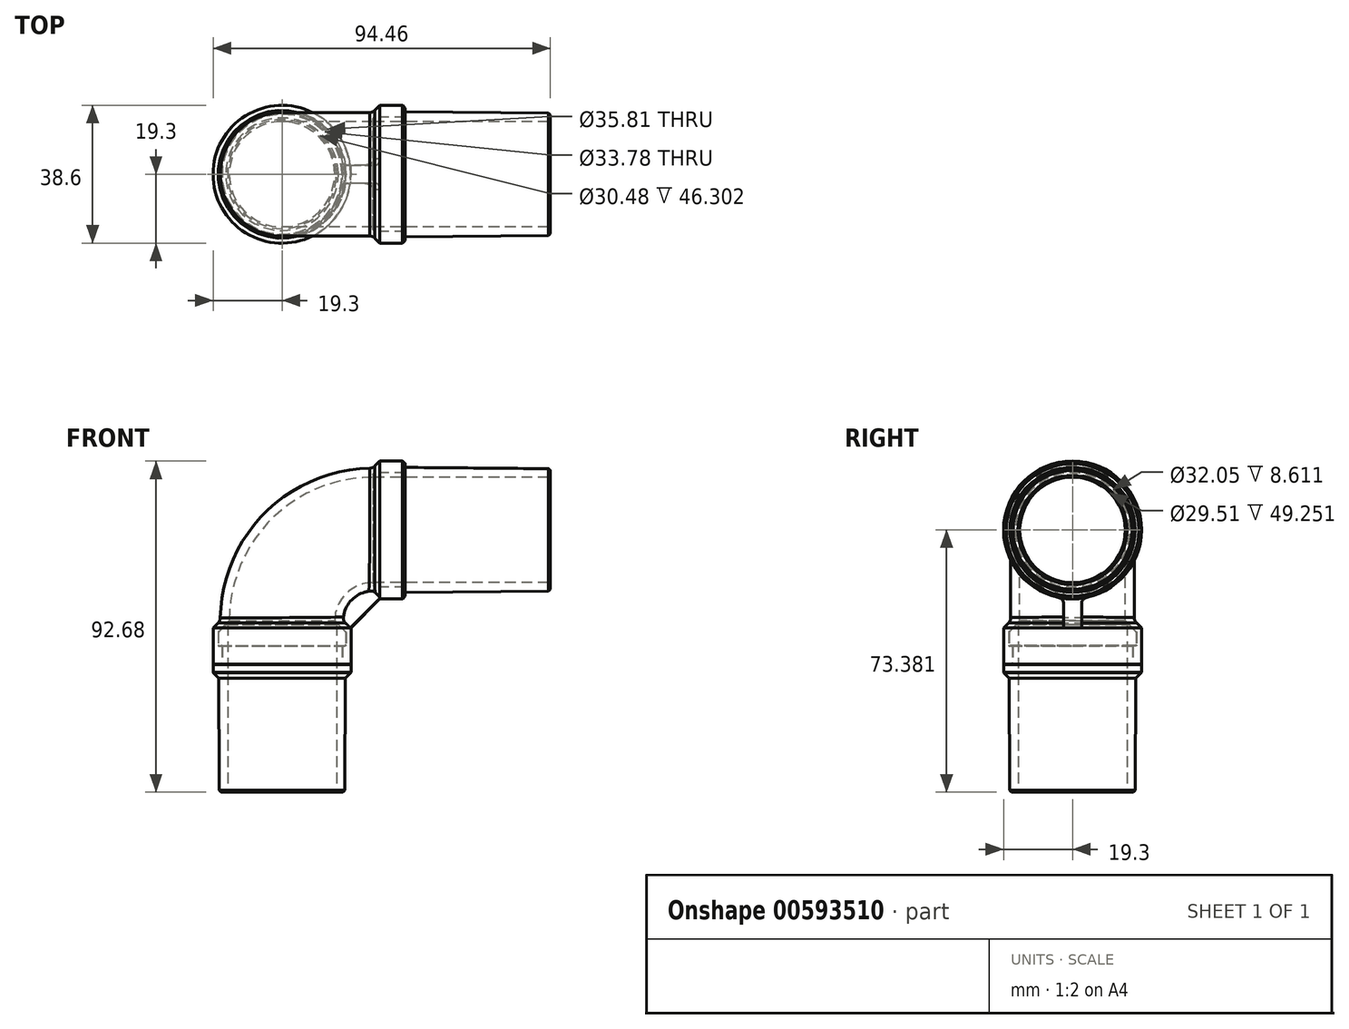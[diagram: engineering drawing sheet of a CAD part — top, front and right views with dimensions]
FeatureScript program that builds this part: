
annotation { "Feature Type Name" : "Feature", "Feature Type Description" : "" }
export const myFeature = defineFeature(function(context is Context, id is Id, definition is map)
    precondition{}
    {
        {
            var Q0;
            Q0=qCreatedBy(makeId("Front.planeOp"),FACE);
            var sketch = newSketch(context, id + "F0", { "sketchPlane" : qUnion([Q0])});
            skLineSegment(sketch, "E0.right", {"start": v(15.24, 0) * mm, "end": v(15.24, 46.81) * mm});
            skLineSegment(sketch, "E1", {"start": v(15.24, 0) * mm, "end": v(17.59, 0) * mm});
            skLineSegment(sketch, "E2.0", {"start": v(19.3, 33.45) * mm, "end": v(19.3, 35.69) * mm});
            skLineSegment(sketch, "E3", {"start": v(16.76, 36.2) * mm, "end": v(16.76, 40.77) * mm});
            skLineSegment(sketch, "E4.0", {"start": v(17.78, 41.15) * mm, "end": v(17.78, 44.62) * mm});
            skLineSegment(sketch, "E5", {"start": v(0, -5.8) * mm, "end": v(0, 47.98) * mm, "construction": true});
            skLineSegment(sketch, "E6", {"start": v(17.72, 31.88) * mm, "end": v(19.3, 33.45) * mm});
            skLineSegment(sketch, "E7.0", {"start": v(16.9, 36.2) * mm, "end": v(16.9, 40.77) * mm});
            skLineSegment(sketch, "E8.0", {"start": v(17.27, 35.81) * mm, "end": v(19.3, 35.81) * mm});
            skLineSegment(sketch, "E9", {"start": v(19.3, 35.81) * mm, "end": v(19.3, 47.98) * mm});
            skLineSegment(sketch, "E10.0", {"start": v(17.9, 41.15) * mm, "end": v(17.9, 44.62) * mm});
            skLineSegment(sketch, "E11", {"start": v(14.76, 47.98) * mm, "end": v(17.76, 44.98) * mm});
            skPoint(sketch, "E12", {"position": v(25.4, 47.98) * mm});
            skLineSegment(sketch, "E13", {"start": v(14.76, 47.98) * mm, "end": v(17.3, 47.98) * mm});
            skLineSegment(sketch, "E14", {"start": v(17.3, 47.98) * mm, "end": v(19.3, 45.97) * mm});
            skArc(sketch, "E15", {"start": v(25.4, 56.08) * mm, "mid": v(19.67, 53.71) * mm, "end": v(17.3, 47.98) * mm});
            skLineSegment(sketch, "E16", {"start": v(25.4, 54.08) * mm, "end": v(25.4, 56.08) * mm, "construction": true});
            skArc(sketch, "E17", {"start": v(25.4, 54.08) * mm, "mid": v(21.09, 52.3) * mm, "end": v(19.3, 47.98) * mm});
            skArc(sketch, "E18", {"start": v(25.4, 73.38) * mm, "mid": v(7.44, 65.94) * mm, "end": v(0, 47.98) * mm, "construction": true});
            skLineSegment(sketch, "E19", {"start": v(25.4, 56.08) * mm, "end": v(27.4, 54.08) * mm});
            skArc(sketch, "E20", {"start": v(14.76, 47.98) * mm, "mid": v(17.87, 55.5) * mm, "end": v(25.4, 58.62) * mm});
            skLineSegment(sketch, "E21", {"start": v(25.4, 54.08) * mm, "end": v(33.76, 54.08) * mm});
            skLineSegment(sketch, "E22", {"start": v(25.4, 58.62) * mm, "end": v(25.4, 56.08) * mm});
            skLineSegment(sketch, "E23.0", {"start": v(25.9, 57.35) * mm, "end": v(34.52, 57.35) * mm});
            skLineSegment(sketch, "E24.trimOffspring", {"start": v(25.4, 57.86) * mm, "end": v(25.4, 73.38) * mm, "construction": true});
            skLineSegment(sketch, "E25", {"start": v(25.4, 73.38) * mm, "end": v(54.57, 73.38) * mm, "construction": true});
            skLineSegment(sketch, "E26", {"start": v(25.4, 57.86) * mm, "end": v(25.9, 57.35) * mm});
            skLineSegment(sketch, "E27.0", {"start": v(17.59, 0) * mm, "end": v(17.72, 31.88) * mm});
            skLineSegment(sketch, "E28.0", {"start": v(34.52, 54.84) * mm, "end": v(34.52, 57.35) * mm});
            skLineSegment(sketch, "E29", {"start": v(34.52, 54.84) * mm, "end": v(33.76, 54.08) * mm});
            skLineSegment(sketch, "E30.0", {"start": v(17.27, 35.69) * mm, "end": v(19.3, 35.69) * mm});
            skLineSegment(sketch, "E31.0", {"start": v(17.02, 40.9) * mm, "end": v(17.65, 40.9) * mm});
            skLineSegment(sketch, "E32.0", {"start": v(17.02, 41.02) * mm, "end": v(17.65, 41.02) * mm});
            skLineSegment(sketch, "E33.0", {"start": v(15.75, 46.81) * mm, "end": v(17.67, 44.89) * mm});
            skLineSegment(sketch, "E34.0", {"start": v(15.75, 46.81) * mm, "end": v(15.24, 46.81) * mm});
            skArc(sketch, "E35.filletArc", {"start": v(16.9, 36.2) * mm, "mid": v(17, 35.93) * mm, "end": v(17.27, 35.81) * mm});
            skArc(sketch, "E36.filletArc", {"start": v(16.76, 36.2) * mm, "mid": v(16.91, 35.84) * mm, "end": v(17.27, 35.69) * mm});
            skArc(sketch, "E37.filletArc", {"start": v(17.02, 41.02) * mm, "mid": v(16.84, 40.95) * mm, "end": v(16.76, 40.77) * mm});
            skArc(sketch, "E38.filletArc", {"start": v(17.02, 40.9) * mm, "mid": v(16.93, 40.86) * mm, "end": v(16.9, 40.77) * mm});
            skArc(sketch, "E39.filletArc", {"start": v(17.65, 41.02) * mm, "mid": v(17.74, 41.06) * mm, "end": v(17.78, 41.15) * mm});
            skArc(sketch, "E40.filletArc", {"start": v(17.65, 40.9) * mm, "mid": v(17.83, 40.97) * mm, "end": v(17.9, 41.15) * mm});
            skPoint(sketch, "E41.visualSharp", {"position": v(17.9, 44.83) * mm});
            skArc(sketch, "E41.filletArc", {"start": v(17.9, 44.62) * mm, "mid": v(17.87, 44.81) * mm, "end": v(17.76, 44.98) * mm});
            skPoint(sketch, "E42.visualSharp", {"position": v(17.78, 44.78) * mm});
            skArc(sketch, "E42.filletArc", {"start": v(17.78, 44.62) * mm, "mid": v(17.75, 44.77) * mm, "end": v(17.67, 44.89) * mm});
            skSolve(sketch);
        }
        {
            var Q0;
            Q0=makeQuery(id+"F0.imprint","IMPRINT",FACE,{"disambiguationData":[TD([[makeQuery(id+"F0.imprint","IMPRINT",EDGE,{"derivedFrom":sQuery(id+"F0.wireOp",EDGE,"E0.right")}),-1.0]])]});
            var Q1;
            Q1=sQuery(id+"F0.wireOp",EDGE,"E5");
            revolve(context, id + "F1", {"entities" : qUnion([Q0]), "axis" : qUnion([Q1]), "revolveType" : RevolveType.FULL});
        }
        {
            var Q0;
            Q0=makeQuery(id+"F1.opRevolve","SWEPT_FACE",FACE,{"disambiguationData":[OSD([sQuery(id+"F0.wireOp",EDGE,"E1")])]});
            chamfer(context, id + "F2", {"entities" : qUnion([Q0]), "width" : 0.5 * mm, "tangentPropagation" : true});
        }
        {
            var Q0;
            Q0=makeQuery(id+"F0.imprint","IMPRINT",FACE,{"disambiguationData":[TD([[makeQuery(id+"F0.imprint","IMPRINT",EDGE,{"derivedFrom":sQuery(id+"F0.wireOp",EDGE,"E7.0")}),-1.0]])]});
            var Q1;
            Q1=sQuery(id+"F0.wireOp",EDGE,"E5");
            revolve(context, id + "F3", {"entities" : qUnion([Q0]), "axis" : qUnion([Q1]), "revolveType" : RevolveType.FULL});
        }
        {
            var Q0;
            Q0=sQuery(id+"F0.wireOp",VERTEX,"E12");
            var Q1;
            Q1=qCreatedBy(makeId("Top.planeOp"),FACE);
            cPlane(context, id + "F4", {"entities" : qUnion([Q0, Q1]), "cplaneType" : CPlaneType.PLANE_POINT, "offset" : 0 * mm, "width" : 152.4 * mm, "height" : 152.4 * mm});
        }
        {
            var Q0;
            Q0=qCreatedBy(id+"F4.planeOp",FACE);
            var sketch = newSketch(context, id + "F5", { "sketchPlane" : qUnion([Q0])});
            skPoint(sketch, "E43.0", {"position": v(25.4, 0) * mm});
            skLineSegment(sketch, "E44", {"start": v(25.4, 0) * mm, "end": v(25.4, 27.74) * mm, "construction": true});
            skLineSegment(sketch, "E45", {"start": v(25.4, 0) * mm, "end": v(44.16, 0) * mm, "construction": true});
            skSolve(sketch);
        }
        {
            var Q0;
            Q0=makeQuery(id+"F3.opRevolve","SWEPT_FACE",FACE,{"disambiguationData":[OSD([sQuery(id+"F0.wireOp",EDGE,"E13")])]});
            var Q1;
            Q1=sQuery(id+"F5.wireOp",EDGE,"E44");
            revolve(context, id + "F6", {"operationType" : NewBodyOperationType.ADD, "entities" : qUnion([Q0]), "axis" : qUnion([Q1]), "revolveType" : RevolveType.ONE_DIRECTION, "angle" : 90 * degree});
        }
        {
            var Q0;
            {var subQ0=sQuery(id+"F0.wireOp",EDGE,"E19");Q0=makeQuery(id+"F0.imprint","IMPRINT",FACE,{"disambiguationData":[TD([[makeQuery(id+"F0.imprint","IMPRINT",EDGE,{"derivedFrom":subQ0}),1.0]])]});}
            var Q1;
            Q1=sQuery(id+"F0.wireOp",EDGE,"E25");
            revolve(context, id + "F7", {"operationType" : NewBodyOperationType.ADD, "entities" : qUnion([Q0]), "axis" : qUnion([Q1]), "revolveType" : RevolveType.FULL});
        }
        {
            var Q0;
            Q0=qCreatedBy(makeId("Front.planeOp"),FACE);
            var sketch = newSketch(context, id + "F8", { "sketchPlane" : qUnion([Q0])});
            skLineSegment(sketch, "E46", {"start": v(25.4, 58.62) * mm, "end": v(75.16, 58.62) * mm});
            skLineSegment(sketch, "E47", {"start": v(34.52, 57.35) * mm, "end": v(25.9, 57.35) * mm});
            skLineSegment(sketch, "E48.0.0", {"start": v(25.4, 58.62) * mm, "end": v(25.4, 57.86) * mm});
            skPoint(sketch, "E49.orphan", {"position": v(28.17, 91.92) * mm});
            skPoint(sketch, "E50.orphan", {"position": v(28.17, 54.84) * mm});
            skLineSegment(sketch, "E51.0", {"start": v(25.4, 57.86) * mm, "end": v(25.9, 57.35) * mm});
            skLineSegment(sketch, "E52.0", {"start": v(34.52, 57.35) * mm, "end": v(34.52, 55.87) * mm});
            skLineSegment(sketch, "E53.0", {"start": v(75.16, 56.24) * mm, "end": v(75.16, 58.62) * mm});
            skLineSegment(sketch, "E54", {"start": v(75.16, 56.24) * mm, "end": v(34.52, 55.87) * mm});
            skSolve(sketch);
        }
        {
            var Q0;
            Q0=makeQuery(id+"F8.imprint","IMPRINT",FACE,{"disambiguationData":[TD([[makeQuery(id+"F8.imprint","IMPRINT",EDGE,{"derivedFrom":sQuery(id+"F8.wireOp",EDGE,"E46")}),-1.0]])]});
            var Q1;
            Q1=sQuery(id+"F0.wireOp",EDGE,"E25");
            revolve(context, id + "F9", {"entities" : qUnion([Q0]), "axis" : qUnion([Q1]), "revolveType" : RevolveType.FULL});
        }
        {
            var Q0;
            Q0=makeQuery(id+"F9.opRevolve","SWEPT_FACE",FACE,{"disambiguationData":[OSD([sQuery(id+"F8.wireOp",EDGE,"E53.0")])]});
            chamfer(context, id + "F10", {"entities" : qUnion([Q0]), "width" : 0.5 * mm, "tangentPropagation" : true});
        }
        {
            var Q0;
            Q0=sQuery(id+"F0.wireOp",EDGE,"E19");
            cPlane(context, id + "F11", {"entities" : qUnion([Q0]), "cplaneType" : CPlaneType.LINE_ANGLE, "offset" : 25.4 * mm, "angle" : 90 * degree, "width" : 152.4 * mm, "height" : 152.4 * mm});
        }
        {
            var Q0;
            Q0=qCreatedBy(id+"F11.planeOp",FACE);
            var sketch = newSketch(context, id + "F12", { "sketchPlane" : qUnion([Q0])});
            skEllipticalArc(sketch, "E55.0", {});
            skLineSegment(sketch, "E56.0", {"start": v(-2.54, 23.65) * mm, "end": v(-2.54, 18.98) * mm});
            skLineSegment(sketch, "E57.0", {"start": v(2.54, 23.65) * mm, "end": v(2.54, 18.98) * mm});
            skEllipticalArc(sketch, "E58.0", {});
            const initialGuessF12  = {"E55.0": [0, 0.032508527184401385, 1, 0, 0.019304, 0.013649989304025105, 4.580427372724815, 4.844350588044565], "E58.0": [0, 0.03392740765153032, 1, 0, 0.014757399999999999, 0.010435057612682356, 4.539410601107297, 4.88536735966208]};
            skSetInitialGuess(sketch, initialGuessF12);
            skSolve(sketch);
        }
        {
            var Q0;
            Q0=makeQuery(id+"F12.imprint","IMPRINT",FACE,{"disambiguationData":[TD([[makeQuery(id+"F12.imprint","IMPRINT",EDGE,{"derivedFrom":sQuery(id+"F12.wireOp",EDGE,"E55.0")}),1.0]])]});
            extrude(context, id + "F13", {"entities" : qUnion([Q0]), "operationType" : NewBodyOperationType.ADD, "depth" : 0.76 * mm, "offsetDistance" : 25.4 * mm});
        }
        {
            var Q0;
            Q0=makeQuery(id+"F12.imprint","IMPRINT",FACE,{"disambiguationData":[TD([[makeQuery(id+"F12.imprint","IMPRINT",EDGE,{"derivedFrom":sQuery(id+"F12.wireOp",EDGE,"E55.0")}),1.0]])]});
            extrude(context, id + "F14", {"entities" : qUnion([Q0]), "operationType" : NewBodyOperationType.ADD, "endBound" : BoundingType.UP_TO_NEXT, "oppositeDirection" : true, "depth" : 25.4 * mm, "offsetDistance" : 25.4 * mm});
        }
        {
            var Q0;
            {var subQ0=sQuery(id+"F12.wireOp",EDGE,"E56.0");Q0=makeQuery(id+"F14.boolean.opBoolean","MERGE",FACE,{"derivedFrom":[makeQuery(id+"F13.opExtrude","SWEPT_FACE",FACE,{"disambiguationData":[OSD([subQ0])]}),makeQuery(id+"F14.opExtrude","SWEPT_FACE",FACE,{"disambiguationData":[OSD([subQ0])]})]});}
            extrude(context, id + "F15", {"entities" : qUnion([Q0]), "operationType" : NewBodyOperationType.ADD, "oppositeDirection" : true, "depth" : 5.08 * mm, "offsetDistance" : 25.4 * mm});
        }
        {
            var Q0;
            Q0=makeQuery(id+"F15.opExtrude","SWEPT_FACE",FACE,{"disambiguationData":[OSD([sQuery(id+"F12.wireOp",EDGE,"E56.0"),sQuery(id+"F12.wireOp",EDGE,"E58.0")])]});
            extrude(context, id + "F16", {"entities" : qUnion([Q0]), "operationType" : NewBodyOperationType.ADD, "endBound" : BoundingType.UP_TO_NEXT, "depth" : 25.4 * mm, "offsetDistance" : 25.4 * mm});
        }
        {
            var Q0;
            {var subQ0=makeQuery(id+"F6.opRevolve","SWEPT_FACE",FACE,{"disambiguationData":[OSD([sQuery(id+"F0.wireOp",EDGE,"E13"),sQuery(id+"F0.wireOp",EDGE,"E14"),sQuery(id+"F0.wireOp",EDGE,"E15")])]});var subQ1=subQ0;var subQ2=sQuery(id+"F12.wireOp",EDGE,"E58.0");var subQ3=sQuery(id+"F12.wireOp",EDGE,"E56.0");Q0=makeQuery(id+"F16.boolean.opBoolean","MERGE",EDGE,{"derivedFrom":[makeQuery(id+"F14.boolean.opBoolean","INTERSECT",EDGE,{"derivedFrom":[subQ1,makeQuery(id+"F14.opExtrude","SWEPT_FACE",FACE,{"disambiguationData":[OSD([subQ3])]})]}),makeQuery(id+"F14.opExtrude","CAP_EDGE",EDGE,{"disambiguationData":[OSD([subQ3]),topologyDisambiguationEdgeConnected([subQ0])],"isStart":false}),makeQuery(id+"F16.opExtrude","TWEAK_EDGE",EDGE,{"derivedFrom":[makeQuery(id+"F15.boolean.opBoolean","MERGE",EDGE,{"derivedFrom":[makeQuery(id+"F14.opExtrude","SWEPT_EDGE",EDGE,{"disambiguationData":[OSD([subQ3,subQ2])]}),makeQuery(id+"F15.opExtrude","CAP_EDGE",EDGE,{"disambiguationData":[OSD([subQ3,subQ2])],"isStart":true})]}),subQ1]})]});}
            var Q1;
            {var subQ0=makeQuery(id+"F6.opRevolve","SWEPT_FACE",FACE,{"disambiguationData":[OSD([sQuery(id+"F0.wireOp",EDGE,"E13"),sQuery(id+"F0.wireOp",EDGE,"E14"),sQuery(id+"F0.wireOp",EDGE,"E15")])]});var subQ1=subQ0;var subQ2=sQuery(id+"F12.wireOp",EDGE,"E58.0");var subQ3=sQuery(id+"F12.wireOp",EDGE,"E57.0");Q1=makeQuery(id+"F16.boolean.opBoolean","MERGE",EDGE,{"derivedFrom":[makeQuery(id+"F14.boolean.opBoolean","INTERSECT",EDGE,{"derivedFrom":[subQ1,makeQuery(id+"F14.opExtrude","SWEPT_FACE",FACE,{"disambiguationData":[OSD([subQ3])]})]}),makeQuery(id+"F14.opExtrude","CAP_EDGE",EDGE,{"disambiguationData":[OSD([subQ3]),topologyDisambiguationEdgeConnected([subQ0])],"isStart":false}),makeQuery(id+"F16.opExtrude","TWEAK_EDGE",EDGE,{"derivedFrom":[makeQuery(id+"F15.boolean.opBoolean","MERGE",EDGE,{"derivedFrom":[makeQuery(id+"F14.opExtrude","SWEPT_EDGE",EDGE,{"disambiguationData":[OSD([subQ3,subQ2])]}),makeQuery(id+"F15.opExtrude","CAP_EDGE",EDGE,{"disambiguationData":[OSD([sQuery(id+"F12.wireOp",EDGE,"E56.0"),subQ2])],"isStart":false})]}),subQ1]})]});}
            var Q2;
            Q2=makeQuery(id+"F13.boolean.opBoolean","INTERSECT",EDGE,{"derivedFrom":[makeQuery(id+"F7.opRevolve","SWEPT_FACE",FACE,{"disambiguationData":[OSD([sQuery(id+"F0.wireOp",EDGE,"E19")])]}),makeQuery(id+"F13.opExtrude","SWEPT_FACE",FACE,{"disambiguationData":[OSD([sQuery(id+"F12.wireOp",EDGE,"E56.0")])]})]});
            var Q3;
            {var subQ0=sQuery(id+"F0.wireOp",EDGE,"E15");Q3=makeQuery(id+"F7.boolean.opBoolean","MERGE",EDGE,{"derivedFrom":[makeQuery(id+"F6.opRevolve","CAP_EDGE",EDGE,{"disambiguationData":[OSD([sQuery(id+"F0.wireOp",EDGE,"E13"),sQuery(id+"F0.wireOp",EDGE,"E14"),subQ0])],"isStart":false}),makeQuery(id+"F7.opRevolve","SWEPT_EDGE",EDGE,{"disambiguationData":[OSD([subQ0,sQuery(id+"F0.wireOp",EDGE,"E19"),sQuery(id+"F0.wireOp",EDGE,"E22")])]})]});}
            var Q4;
            {var subQ0=sQuery(id+"F0.wireOp",EDGE,"E15");var subQ1=sQuery(id+"F0.wireOp",EDGE,"E14");var subQ2=sQuery(id+"F0.wireOp",EDGE,"E13");Q4=makeQuery(id+"F6.boolean.opBoolean","MERGE",EDGE,{"derivedFrom":[makeQuery(id+"F3.opRevolve","SWEPT_EDGE",EDGE,{"disambiguationData":[OSD([subQ2,subQ1,subQ0])]}),makeQuery(id+"F6.opRevolve","CAP_EDGE",EDGE,{"disambiguationData":[OSD([subQ2,subQ1,subQ0])],"isStart":true})]});}
            var Q5;
            Q5=makeQuery(id+"F13.boolean.opBoolean","INTERSECT",EDGE,{"derivedFrom":[makeQuery(id+"F7.opRevolve","SWEPT_FACE",FACE,{"disambiguationData":[OSD([sQuery(id+"F0.wireOp",EDGE,"E19")])]}),makeQuery(id+"F13.opExtrude","SWEPT_FACE",FACE,{"disambiguationData":[OSD([sQuery(id+"F12.wireOp",EDGE,"E57.0")])]})]});
            var Q6;
            Q6=makeQuery(id+"F14.opExtrude","CAP_EDGE",EDGE,{"disambiguationData":[OSD([sQuery(id+"F12.wireOp",EDGE,"E57.0")]),topologyDisambiguationEdgeConnected([makeQuery(id+"F3.opRevolve","SWEPT_FACE",FACE,{"disambiguationData":[OSD([sQuery(id+"F0.wireOp",EDGE,"E14")])]})])],"isStart":false});
            var Q7;
            Q7=makeQuery(id+"F14.opExtrude","CAP_EDGE",EDGE,{"disambiguationData":[OSD([sQuery(id+"F12.wireOp",EDGE,"E56.0")]),topologyDisambiguationEdgeConnected([makeQuery(id+"F3.opRevolve","SWEPT_FACE",FACE,{"disambiguationData":[OSD([sQuery(id+"F0.wireOp",EDGE,"E14")])]})])],"isStart":false});
            fillet(context, id + "F17", {"entities" : qUnion([Q0, Q1, Q2, Q3, Q4, Q5, Q6, Q7]), "radius" : 2.03 * mm, "tangentPropagation" : true, "allowEdgeOverflow" : false});
        }
        {
            var Q0;
            Q0=makeQuery(id+"F1.opRevolve","SWEPT_EDGE",EDGE,{"disambiguationData":[OSD([sQuery(id+"F0.wireOp",EDGE,"E2.0"),sQuery(id+"F0.wireOp",EDGE,"E6")])]});
            var Q1;
            Q1=makeQuery(id+"F7.opRevolve","SWEPT_EDGE",EDGE,{"disambiguationData":[OSD([sQuery(id+"F0.wireOp",EDGE,"E21"),sQuery(id+"F0.wireOp",EDGE,"E29")])]});
            chamfer(context, id + "F18", {"entities" : qUnion([Q0, Q1]), "width" : 0.25 * mm, "tangentPropagation" : true});
        }
    });
